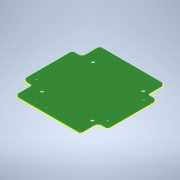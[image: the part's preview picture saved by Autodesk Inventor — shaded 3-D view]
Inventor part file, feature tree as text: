
AUTODESK INVENTOR PART (.ipt)
format: ipt  version: 2021 (Build 250183000, 183)  size: 724,480 bytes
history: native  units: mm
features: sketch x6, projected_geometry x6, other x4, extrude x3, hole x2, fillet x2, reference x1
ambient origin geometry x8: Origin, YZ Plane, XZ Plane, XY Plane, X Axis, Y Axis, Z Axis, Center Point
bodies: Solid1 (feature_tree)
feature tree (24):
  extrude  "Extrusion1"  Depth=95.0mm
  hole  "Hole1"  [1 undecoded]
  extrude  "Extrusion2"  Depth=11.0mm
  fillet  "Fillet1"  Radius=20.0mm
  fillet  "Fillet2"  Radius=20.0mm
  sketch  "Sketch5"  dims[d9=3.0mm d10=6.0mm d11=6.0mm d12=0.1mm d13=90.0deg d14=8.0mm d15=20.594885mm d18=11.0mm d19=20.0mm d21=20.0mm]
  hole  "Hole2"  [1 undecoded]
  extrude  "Extrusion3"  Depth=11.0mm
  sketch  "Sketch1"  dims[d0=95.0mm d1=95.0mm]
  sketch  "Sketch2"  dims[d2=1.6mm d3=0.0mm d7=80.79mm]
  sketch  "Sketch4"  dims[d8=40.942mm]
  reference  "Reference2"
  sketch  "Sketch6"  dims[d22=11.0mm d23=11.0mm]
  sketch  "Sketch7"  dims[d24=20.0mm d25=11.0mm d26=20.0mm d27=1.6mm d28=0.0mm d29=4.0mm d30=3.0mm d31=57.0mm d32=58.0mm d33=4.2mm d34=6.0mm d35=4.0mm d36=2.0mm d37=90.0deg d38=8.0mm d39=20.594885mm d41=3.0mm d42=10.0mm d43=0.0mm]
  other  "<userpath>\OneDrive\Dokumenty\GitHub\escape_room_hw_v2\Enclosure\Product.iam"
  other  "Product.iam"
  other  "zp105_105_75jph_tm:1"
  other  "zp105_105_75jph_tm_Temp_6:1"
  projected_geometry  "Project Cut Edges1"
  projected_geometry  "Project Cut Edges2"
  projected_geometry  "Project Cut Edges3"
  projected_geometry  "Project Cut Edges4"
  projected_geometry  "Project Cut Edges5"
  projected_geometry  "Project Cut Edges6"
note: 2 required parameter values undecoded (feature->parameter linkage not recoverable at this tier; creation-order binding heuristic only, values carry confidence <= 0.55)
